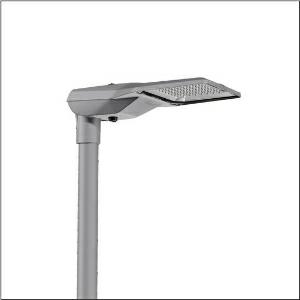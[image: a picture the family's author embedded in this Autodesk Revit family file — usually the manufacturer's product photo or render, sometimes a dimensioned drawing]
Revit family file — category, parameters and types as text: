
# Revit family: streetlight_sl_21_midi___stw1_0a_5xe3e33t08lb_0cd5
name_source: partatom
category: Lighting Fixtures
units: mm (PartAtom-declared; Revit-internal decimal feet)

## family parameters
Cut with Voids When Loaded = No
Host = Face
Light Source = No
Part Type = Normal
Room Calculation Point = No
Round Connector Dimension = Use Diameter
Shared = No

## types (1)
- --- (1 x LED, 14340 lm, 99.6 W, 3000K)
    Apparent Load = 100 VA
    CIE Flux Codes = 38 75 98 100 100
    Color Rendering = 70
    Color Temperature = 3000K
    Default Elevation = 1800 mm
    Description = Streetlight SL 21 midi, mast luminaire, primary light control with lens, of PMMA, primary optical cover: cover, of toughened safety glass, transparent, light distribution: STW1.0a, light emission: direct distribution, primary light characteristic: asymmetric, installation type: side-entry, post-top, LED, High Power LED, rated luminous flux: 14.340lm, luminous efficacy: 144lm/W, light colour: 730, colour temperature: 3000K, control gear: D4i, control: overheat protection, constant luminous flux control, time-dependent luminous flux control, flexible luminous flux parameterisation, pre-setting: logarithmic dimming characteristic, mains connection: 230..240V, AC, 50/60Hz, start of lifetime: 100W, end of service life: 102W, reduction: 46W, luminaire housing, of diecast aluminium, powder-coated, SITECO metallic grey (DB 702S), corrosivity category C5 high according to DIN EN ISO 12944, please order mast flange separately, inclination adjustable: 0°, 5°, 10°, 15°, sealing non-destructively replaceable, multi-level sealing system, length: 644mm, width: 335mm, height: 110mm, mast flange for spigot size: 42mm (side-entry): 5XC10008XM4, 60/48mm (side-entry/post-top): 5XC10108XM2, 76/60mm (side-entry/post-top): 5XC10108XM1, mounting height: 4..8m, Smart Interface below and above, protection rating (complete): IP66, insulation class (complete): insulation class II (safety insulation), certification: CE, ENEC, ENEC+, VDE, impact resistance: IK10, permissible operating ambient temperature for outdoor applications: -40..+50°C, standard-compliant lighting for roads and squares, packaging unit: 1 piece

Light Distribution: STW1.0a
    Height = 111 mm
    Lamp = 1 x LED
    Lamp Light Flux = 14340 lm
    Lamp Power = 99.6 W
    Lamp count = 1
    Length = 644 mm
    Luminous efficacy = 144 lm/W
    Manufacturer = Siteco
    ModVariant = No
    Model = 5XE3E33T08LB
    Number of Poles = 1
    OnlyDefault = Yes
    Power Factor = 1
    Product Name = Streetlight SL 21 midi | STW1.0a
    Product group = mast luminaire | pylon top
    ProductGroupID = 6100
    Protection Class = Protection class II
    Protection Degree = IP 66
    RLX_Detail_Level = 1
    RLX_Emergency_Light_Flux = 0 lm
    RLX_Emergency_Type = 0
    RLX_Emergency_Type_DB = No
    RlxData = <blob elided: 26933 chars, md5=9725e627>
    Socket = socket
    Standby Power = 0 W
    System Light Flux = 14340 lm
    System Power = 100 W
    Type Comments = factory setting: luminous flux: 100 % | dim-lin: 254 | 1020 mA
    Type Image = l_1004304.jpg
    URL = http://relux.com
    VarID = @adj_031425
    Voltage = 0 V
    Weight = 0.00 kg
    Width = 336 mm

## geometry (parser evidence)
native form markers: Blend x4, Sweep x12
no freeform markers — native parametric forms only
